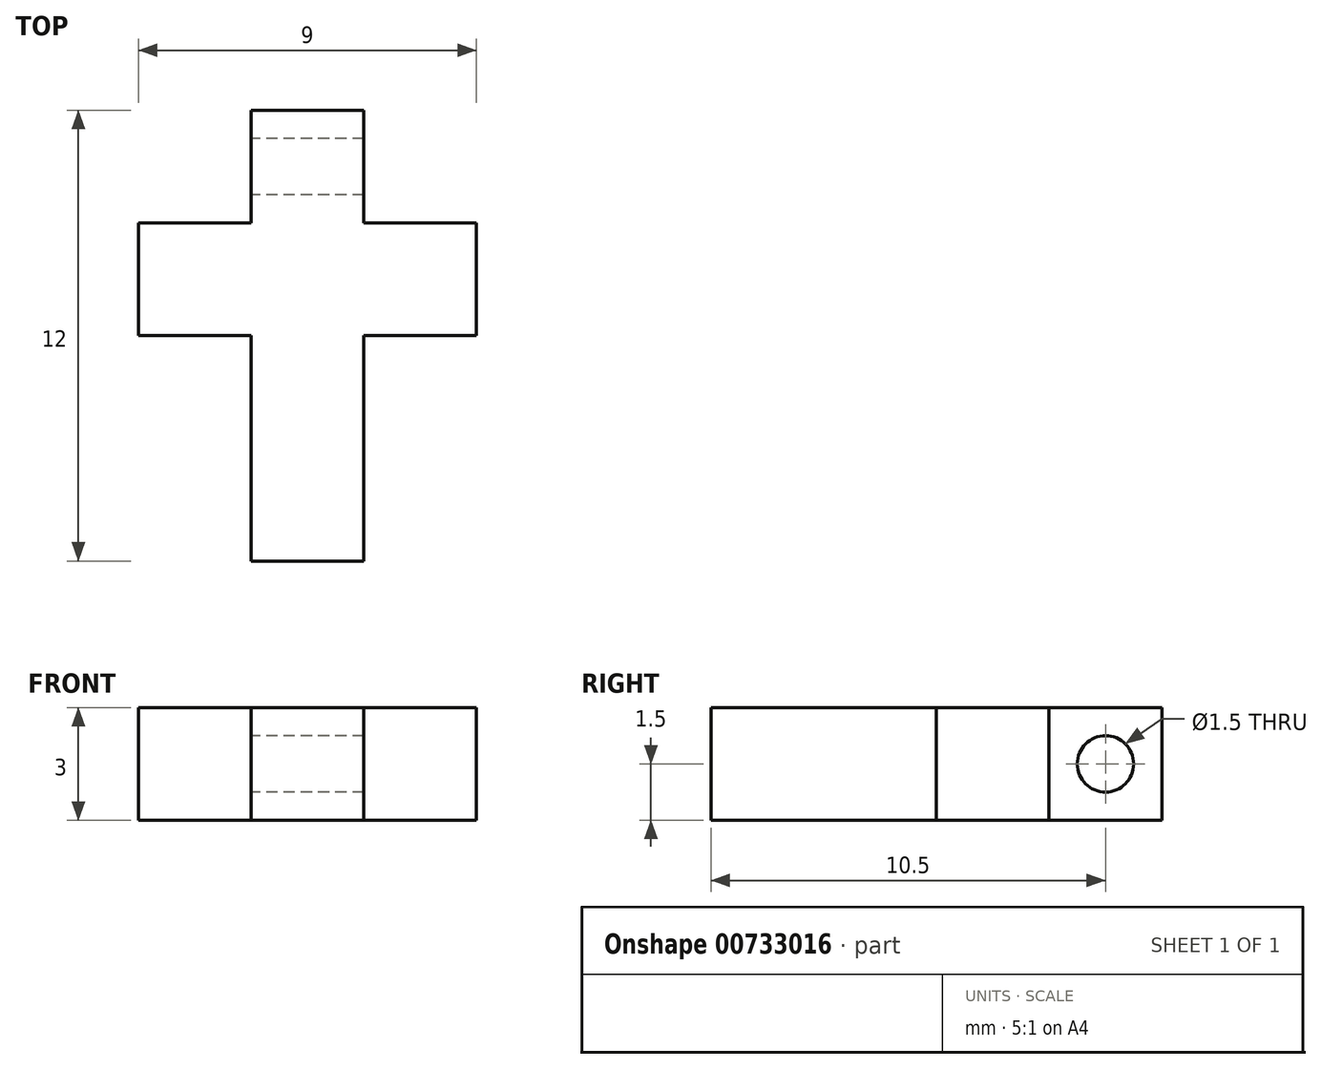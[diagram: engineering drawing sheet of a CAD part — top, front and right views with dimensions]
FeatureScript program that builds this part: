
annotation { "Feature Type Name" : "Feature", "Feature Type Description" : "" }
export const myFeature = defineFeature(function(context is Context, id is Id, definition is map)
    precondition{}
    {
        {
            var Q0;
            Q0=qCreatedBy(makeId("Top.planeOp"),FACE);
            var sketch = newSketch(context, id + "F0", { "sketchPlane" : qUnion([Q0])});
            skLineSegment(sketch, "E0.bottom", {"start": v(4.5, 1.5) * mm, "end": v(-4.5, 1.5) * mm});
            skLineSegment(sketch, "E0.top", {"start": v(4.5, -1.5) * mm, "end": v(-4.5, -1.5) * mm});
            skLineSegment(sketch, "E0.left", {"start": v(4.5, 1.5) * mm, "end": v(4.5, -1.5) * mm});
            skLineSegment(sketch, "E0.right", {"start": v(-4.5, 1.5) * mm, "end": v(-4.5, -1.5) * mm});
            skPoint(sketch, "E0.middle", {"position": v(0, 0) * mm});
            skLineSegment(sketch, "E1.bottom", {"start": v(-1.5, 4.5) * mm, "end": v(1.5, 4.5) * mm});
            skLineSegment(sketch, "E1.top", {"start": v(-1.5, -7.5) * mm, "end": v(1.5, -7.5) * mm});
            skLineSegment(sketch, "E1.left", {"start": v(-1.5, 4.5) * mm, "end": v(-1.5, -7.5) * mm});
            skLineSegment(sketch, "E1.right", {"start": v(1.5, 4.5) * mm, "end": v(1.5, -7.5) * mm});
            skLineSegment(sketch, "E2", {"start": v(-1.5, 13.6) * mm, "end": v(0, 13.6) * mm, "construction": true});
            skLineSegment(sketch, "E3", {"start": v(1.5, 13.6) * mm, "end": v(0, 13.6) * mm, "construction": true});
            skSolve(sketch);
        }
        {
            var Q0;
            {var subQ5=sQuery(id+"F0.wireOp",EDGE,"E1.bottom");Q0=makeQuery(id+"F0.imprint","IMPRINT",FACE,{"disambiguationData":[TD([[makeQuery(id+"F0.imprint","IMPRINT",EDGE,{"derivedFrom":subQ5}),-1.0]])]});}
            var Q1;
            {var subQ0=sQuery(id+"F0.wireOp",EDGE,"E1.right");var subQ1=sQuery(id+"F0.wireOp",EDGE,"E0.bottom");var subQ2=makeQuery(id+"F0.imprint","INTERSECT",VERTEX,{"derivedFrom":[subQ1,subQ0]});Q1=makeQuery(id+"F0.imprint","IMPRINT",FACE,{"disambiguationData":[TD([[makeQuery(id+"F0.imprint","IMPRINT",EDGE,{"disambiguationData":[TD([[subQ2,-1.0]])],"derivedFrom":subQ1}),1.0]])]});}
            var Q2;
            {var subQ0=sQuery(id+"F0.wireOp",EDGE,"E0.right");Q2=makeQuery(id+"F0.imprint","IMPRINT",FACE,{"disambiguationData":[TD([[makeQuery(id+"F0.imprint","IMPRINT",EDGE,{"derivedFrom":subQ0}),1.0]])]});}
            var Q3;
            {var subQ5=sQuery(id+"F0.wireOp",EDGE,"E1.top");Q3=makeQuery(id+"F0.imprint","IMPRINT",FACE,{"disambiguationData":[TD([[makeQuery(id+"F0.imprint","IMPRINT",EDGE,{"derivedFrom":subQ5}),1.0]])]});}
            var Q4;
            {var subQ0=sQuery(id+"F0.wireOp",EDGE,"E0.left");Q4=makeQuery(id+"F0.imprint","IMPRINT",FACE,{"disambiguationData":[TD([[makeQuery(id+"F0.imprint","IMPRINT",EDGE,{"derivedFrom":subQ0}),-1.0]])]});}
            extrude(context, id + "F1", {"entities" : qUnion([Q0, Q1, Q2, Q3, Q4]), "depth" : 3 * mm, "offsetDistance" : 25 * mm});
        }
        {
            var Q0;
            {var subQ0=sQuery(id+"F0.wireOp",EDGE,"E1.left");Q0=makeQuery(id+"F1.opExtrude","SWEPT_FACE",FACE,{"disambiguationData":[OSD([subQ0]),TDD([makeQuery(id+"F0.imprint","IMPRINT",EDGE,{"disambiguationData":[TD([[makeQuery(id+"F0.imprint","INTERSECT",VERTEX,{"derivedFrom":[sQuery(id+"F0.wireOp",EDGE,"E1.bottom"),subQ0]}),-1.0]])],"derivedFrom":subQ0})])]});}
            var sketch = newSketch(context, id + "F2", { "sketchPlane" : qUnion([Q0])});
            skCircle(sketch, "E4", {"center": v(-3, 1.5) * mm, "radius": 0.75 * mm});
            skPoint(sketch, "E4.centerSnap0", {"position": v(-4.5, 1.5) * mm});
            skPoint(sketch, "E4.centerSnap1", {"position": v(-3, 3) * mm});
            skSolve(sketch);
        }
        {
            var Q0;
            Q0=makeQuery(id+"F2.imprint","IMPRINT",FACE,{"disambiguationData":[TD([[makeQuery(id+"F2.imprint","IMPRINT",EDGE,{"derivedFrom":sQuery(id+"F2.wireOp",EDGE,"E4")}),1.0]])]});
            extrude(context, id + "F3", {"entities" : qUnion([Q0]), "operationType" : NewBodyOperationType.REMOVE, "oppositeDirection" : true, "depth" : 25 * mm, "offsetDistance" : 25 * mm});
        }
    });
